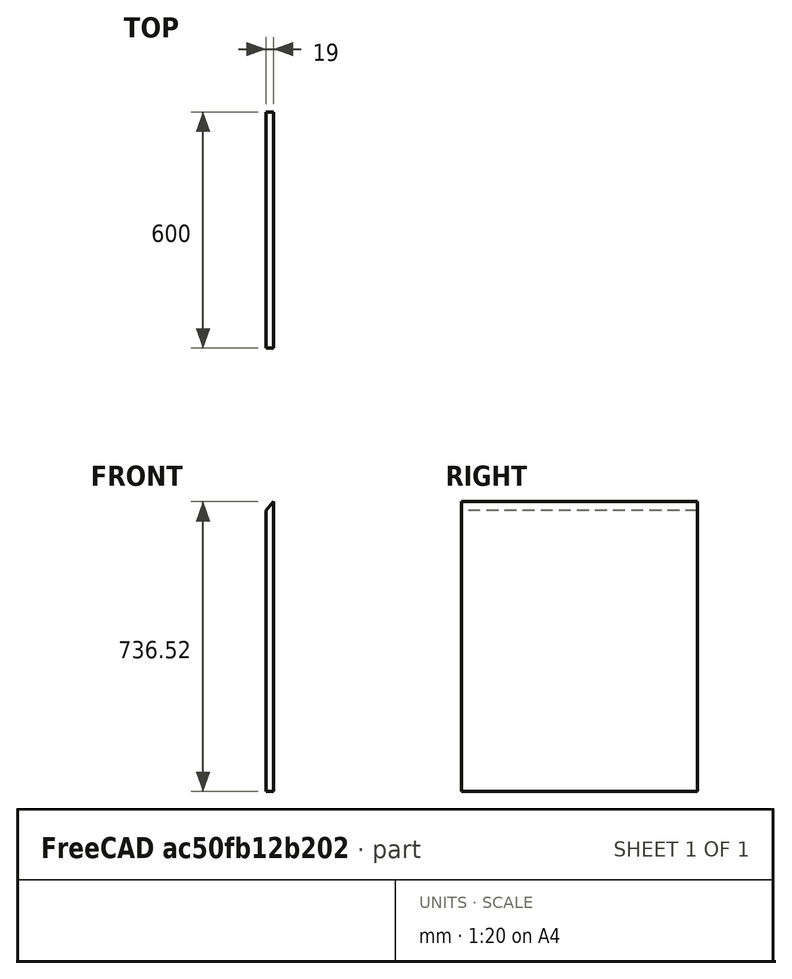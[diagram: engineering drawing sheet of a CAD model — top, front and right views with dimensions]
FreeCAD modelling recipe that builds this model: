
FCSTD DOCUMENT  (FreeCAD 1.0RUnknown)
Label: wardrobe_right_corpus03_jan
License: All rights reserved
LicenseURL: https://en.wikipedia.org/wiki/All_rights_reserved
objects: TechDraw::DrawViewDimension×4, PartDesign::CoordinateSystem×2, TechDraw::DrawProjGroupItem×2, Sketcher::SketchObject×1, PartDesign::Pad×1, PartDesign::Body×1, App::Part×1, TechDraw::DrawSVGTemplate×1, TechDraw::DrawPage×1
note: 14 computed .brp shape members not serialized (recipe doc carries the construction recipe); baked Part::Feature solids carry a one-line shape summary decoded from their .brp
EXTERNAL_REF file=../../mastersheet.FCStd obj=Spreadsheet
EXTERNAL_REF file=../../mastersketch.FCStd obj=Sketch
EXTERNAL_REF file=../../mastersketch.FCStd obj=Sketch001

FEATURE [Sketcher::SketchObject] Sketch
  ArcFitTolerance = 1e-06
  AttachmentSupport = -> [XZ_Plane004]
  FullyConstrained = true
  MakeInternals = false
  MapMode = 5
  Placement = pos=(0,0,0) rot=(1,0,0;1.5708rad)
  expr: Constraints[10] = mastersketch#<<corpus>>.Constraints.corpus03_right_height
  expr: Constraints[6] = mastersheet#Spreadsheet.corpus_outer_thickness
  expr: Constraints[9] = mastersketch#Sketch.Constraints.alpha
  sketch-geometry (4):
    g0: LineSegment StartX=0 StartY=0 StartZ=0 EndX=0 EndY=736.518 EndZ=0
    g1: LineSegment StartX=-19 StartY=714.286 StartZ=0 EndX=-19 EndY=0 EndZ=0
    g2: LineSegment StartX=-19 StartY=0 StartZ=0 EndX=0 EndY=0 EndZ=0
    g3: LineSegment StartX=0 StartY=736.518 StartZ=0 EndX=-19 EndY=714.286 EndZ=0
  constraints (11):
    c: Coincident(g1,g2)
    c: Coincident(g2,g0)
    c: Vertical(g0)
    c: Vertical(g1)
    c: Horizontal(g2)
    c: Coincident(g0,g-1)
    c: DistanceX(g2,g2) = 19
    c: Coincident(g3,g0)
    c: Coincident(g1,g3)
    c: Angle(g1,g3) = 2.43442
    c: DistanceY(g0,g0) = 736.518
FEATURE [PartDesign::Pad] Pad
  Direction = (0,-1,2e-16)
  Length = 600
  Length2 = 10
  Placement = pos=(0,0,0) rot=(1,0,0;1.5708rad)
  Profile = -> Sketch
  ReferenceAxis = -> Sketch [N_Axis]
  Refine = true
  Suppressed = false
  Type = 0
  expr: Length = mastersheet#Spreadsheet.corpus_depth
FEATURE [PartDesign::Body] Body002  label="wardrobe_right_corpus03_jan"
  AllowCompound = false
  Group = -> [Sketch,Pad]
  Origin = -> Origin004
  Tip = -> Pad
FEATURE [PartDesign::CoordinateSystem] LCS_1
  AttacherType = Attacher::AttachEngine3D
  AttachmentSupport = -> [Pad]
  MapMode = 45
  Placement = pos=(0,-300,6.66e-14) rot=(0,0.707107,0.707107;3.14159rad)
FEATURE [PartDesign::CoordinateSystem] LCS_Origin
  AttacherType = Attacher::AttachEngine3D
  AttachmentSupport = -> [X_Axis]
  MapMode = 2
FEATURE [App::Part] wardrobe_right_corpus03_jan  label="wardrobe_right_corpus03_jan001"
  DrawingName = wardrobe_right_corpus03_jan.FCStd
  Group = -> [LCS_Origin,Body002,LCS_1]
  Origin = -> Origin
  PartDescription = wardrobe_right_corpus03_jan
  PartID = wardrobe_right_corpus03_jan
FEATURE [TechDraw::DrawSVGTemplate] Template  label="Vorlage"
  Height = 210
  Orientation = 1
  Template = <userpath>/scoop/apps/freecad/current/data/Mod/TechDraw/Templates/A4_Landscape_TD.svg
  Width = 297
FEATURE [TechDraw::DrawProjGroupItem] View
  CoarseView = false
  Direction = (-2e-16,1,0)
  Focus = 100
  HardHidden = false
  IsoCount = 0
  IsoHidden = false
  IsoVisible = false
  LockPosition = false
  Perspective = false
  Rotation = 0
  RotationVector = (1,0,0)
  Scale = 0.1
  ScaleType = 2
  ScrubCount = 1
  SeamHidden = false
  SeamVisible = false
  SmoothHidden = false
  SmoothVisible = true
  Source = -> [Body002]
  Type = 0
  X = 207.757
  XDirection = (-1,-2e-16,0)
  Y = 132.115
FEATURE [TechDraw::DrawProjGroupItem] View001
  CoarseView = false
  Direction = (-1,-1e-16,0)
  Focus = 100
  HardHidden = false
  IsoCount = 0
  IsoHidden = false
  IsoVisible = false
  LockPosition = false
  Perspective = false
  Rotation = 0
  RotationVector = (1,0,0)
  Scale = 0.1
  ScaleType = 2
  ScrubCount = 1
  SeamHidden = false
  SeamVisible = false
  SmoothHidden = false
  SmoothVisible = true
  Source = -> [Body002]
  Type = 0
  X = 107.559
  XDirection = (1e-16,-1,0)
  Y = 132.115
FEATURE [TechDraw::DrawViewDimension] Dimension  label="Maß"
  AngleOverride = false
  Arbitrary = false
  ArbitraryTolerances = false
  BoxCorners = (2) [(-30,-36.8259,0),(30,36.8259,0)]
  EqualTolerance = true
  ExtensionAngle = 0
  FormatSpec = %.1w
  FormatSpecOverTolerance = %+.1w
  FormatSpecUnderTolerance = %+.1w
  Inverted = false
  LineAngle = 0
  LockPosition = false
  MeasureType = 1
  OverTolerance = 0
  References2D = -> [View001]
  Rotation = 0
  ScaleType = 0
  TheoreticalExact = false
  Type = 1
  UnderTolerance = 0
  X = 0
  Y = -42.401
FEATURE [TechDraw::DrawViewDimension] Dimension001  label="Maß001"
  AngleOverride = false
  Arbitrary = false
  ArbitraryTolerances = false
  BoxCorners = (2) [(-30,-36.8259,0),(30,36.8259,0)]
  EqualTolerance = true
  ExtensionAngle = 0
  FormatSpec = %.1w
  FormatSpecOverTolerance = %+.1w
  FormatSpecUnderTolerance = %+.1w
  Inverted = false
  LineAngle = 0
  LockPosition = false
  MeasureType = 1
  OverTolerance = 0
  References2D = -> [View001]
  Rotation = 0
  ScaleType = 0
  TheoreticalExact = false
  Type = 0
  UnderTolerance = 0
  X = 43.6616
  Y = 0
FEATURE [TechDraw::DrawViewDimension] Dimension002  label="Maß002"
  AngleOverride = false
  Arbitrary = false
  ArbitraryTolerances = false
  BoxCorners = (2) [(-0.95,-36.8259,0),(0.95,36.8259,0)]
  EqualTolerance = true
  ExtensionAngle = 0
  FormatSpec = %.1w
  FormatSpecOverTolerance = %+.1w
  FormatSpecUnderTolerance = %+.1w
  Inverted = false
  LineAngle = 0
  LockPosition = false
  MeasureType = 1
  OverTolerance = 0
  References2D = -> [View]
  Rotation = 0
  ScaleType = 0
  TheoreticalExact = false
  Type = 0
  UnderTolerance = 0
  X = 12.357
  Y = -45.6451
FEATURE [TechDraw::DrawViewDimension] Dimension003  label="Maß003"
  AngleOverride = false
  Arbitrary = false
  ArbitraryTolerances = false
  BoxCorners = (2) [(-0.95,-36.8259,0),(0.95,36.8259,0)]
  EqualTolerance = true
  ExtensionAngle = 0
  FormatSpec = %.1w
  FormatSpecOverTolerance = %+.1w
  FormatSpecUnderTolerance = %+.1w
  Inverted = false
  LineAngle = 0
  LockPosition = false
  MeasureType = 1
  OverTolerance = 0
  References2D = -> [View]
  Rotation = 0
  ScaleType = 0
  TheoreticalExact = false
  Type = 6
  UnderTolerance = 0
  X = 14.3684
  Y = 3.37588
FEATURE [TechDraw::DrawPage] Page  label="Seite"
  KeepUpdated = true
  NextBalloonIndex = 1
  ProjectionType = 0
  Template = -> Template
  Views = -> [View,View001,Dimension,Dimension001,Dimension002,Dimension003]
